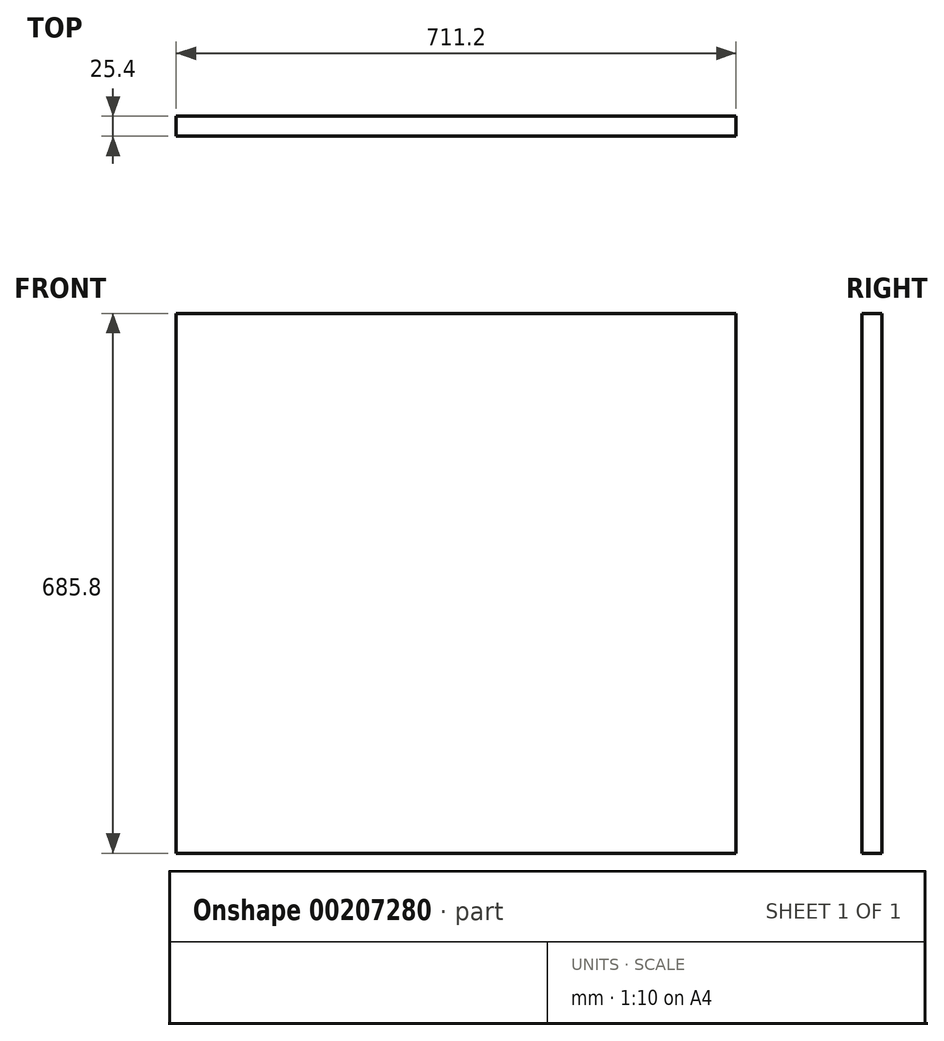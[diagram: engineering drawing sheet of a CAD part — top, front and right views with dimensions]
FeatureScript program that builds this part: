
annotation { "Feature Type Name" : "Feature", "Feature Type Description" : "" }
export const myFeature = defineFeature(function(context is Context, id is Id, definition is map)
    precondition{}
    {
        {
            var Q0;
            Q0=qCreatedBy(makeId("Front.planeOp"),FACE);
            var sketch = newSketch(context, id + "F0", { "sketchPlane" : qUnion([Q0])});
            skLineSegment(sketch, "E0.bottom", {"start": v(-355.6, 342.9) * mm, "end": v(355.6, 342.9) * mm});
            skLineSegment(sketch, "E0.top", {"start": v(-355.6, -342.9) * mm, "end": v(355.6, -342.9) * mm});
            skLineSegment(sketch, "E0.left", {"start": v(-355.6, 342.9) * mm, "end": v(-355.6, -342.9) * mm});
            skLineSegment(sketch, "E0.right", {"start": v(355.6, 342.9) * mm, "end": v(355.6, -342.9) * mm});
            skPoint(sketch, "E0.middle", {"position": v(0, 0) * mm});
            skSolve(sketch);
        }
        {
            var Q0;
            Q0 = qSketchRegion(id + "F0", true);
            extrude(context, id + "F1", {"entities" : qUnion([Q0]), "endBound" : BoundingType.SYMMETRIC, "depth" : 25.4 * mm});
        }
    });
